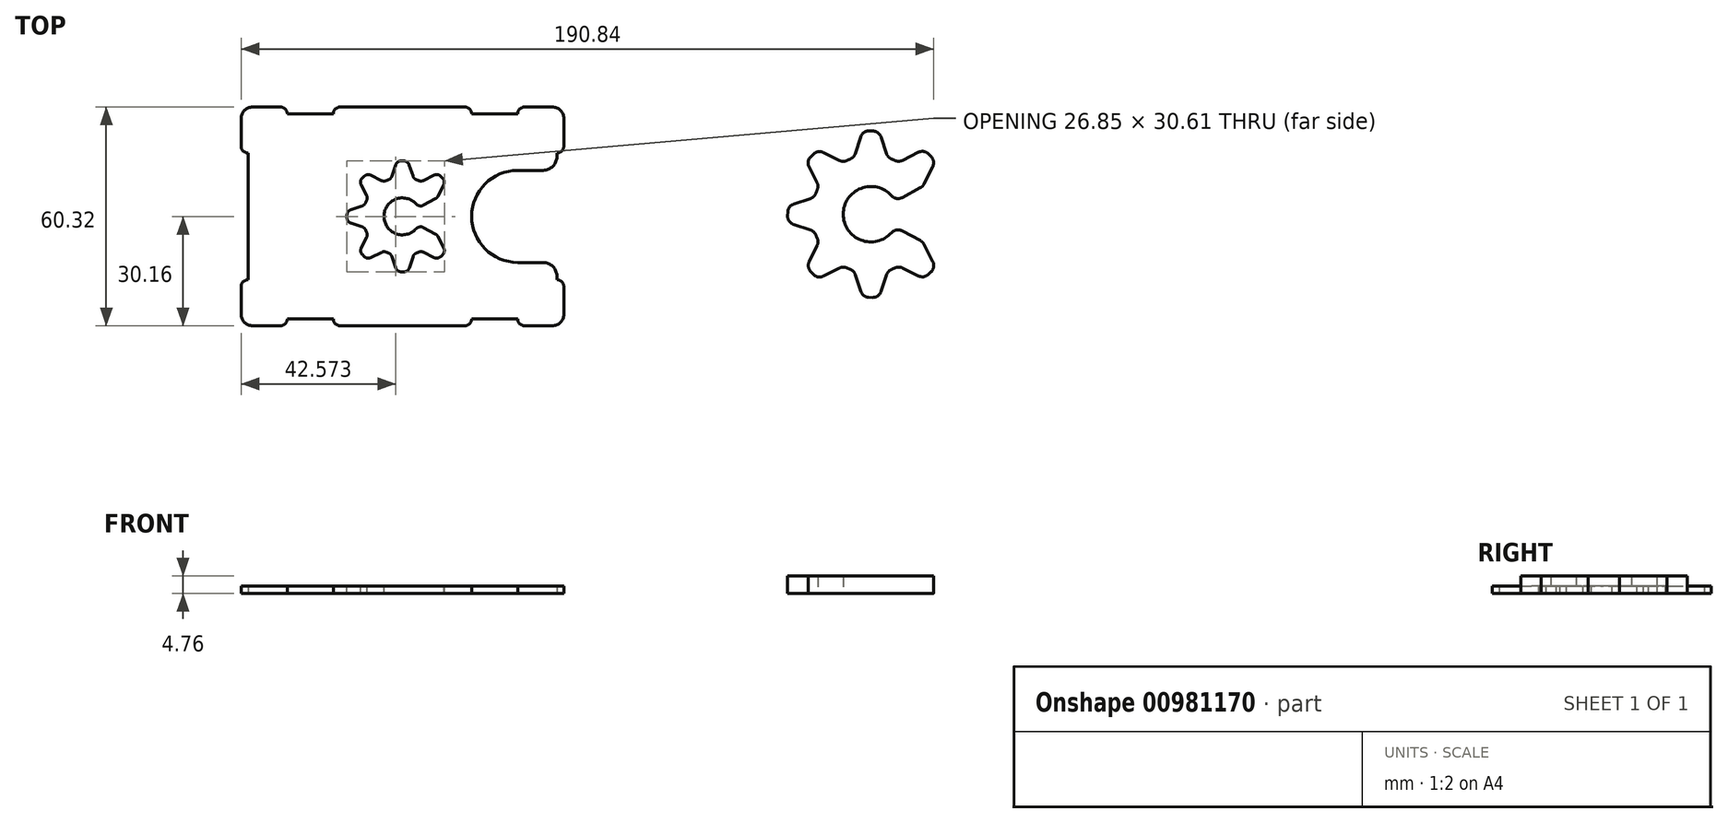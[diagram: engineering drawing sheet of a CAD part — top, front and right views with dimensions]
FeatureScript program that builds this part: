
annotation { "Feature Type Name" : "Feature", "Feature Type Description" : "" }
export const myFeature = defineFeature(function(context is Context, id is Id, definition is map)
    precondition{}
    {
        {
            var Q0;
            Q0=qCreatedBy(makeId("Top.planeOp"),FACE);
            var sketch = newSketch(context, id + "F0", { "sketchPlane" : qUnion([Q0])});
            skLineSegment(sketch, "E0.bottom", {"start": v(39.69, -26.99) * mm, "end": v(-39.69, -26.99) * mm, "construction": true});
            skLineSegment(sketch, "E0.top", {"start": v(39.69, 26.99) * mm, "end": v(-39.69, 26.99) * mm, "construction": true});
            skLineSegment(sketch, "E0.left", {"start": v(42.86, -23.81) * mm, "end": v(42.86, 23.81) * mm, "construction": true});
            skLineSegment(sketch, "E0.right", {"start": v(-42.86, -23.81) * mm, "end": v(-42.86, 23.81) * mm, "construction": true});
            skPoint(sketch, "E0.middle", {"position": v(0, 0) * mm});
            skPoint(sketch, "E1.visualSharp", {"position": v(-42.86, 26.99) * mm});
            skArc(sketch, "E1.filletArc", {"start": v(-39.69, 26.99) * mm, "mid": v(-41.93, 26.06) * mm, "end": v(-42.86, 23.81) * mm, "construction": true});
            skPoint(sketch, "E2.visualSharp", {"position": v(42.86, 26.99) * mm});
            skArc(sketch, "E2.filletArc", {"start": v(42.86, 23.81) * mm, "mid": v(41.93, 26.06) * mm, "end": v(39.69, 26.99) * mm, "construction": true});
            skPoint(sketch, "E3.visualSharp", {"position": v(42.86, -26.99) * mm});
            skArc(sketch, "E3.filletArc", {"start": v(39.69, -26.99) * mm, "mid": v(41.93, -26.06) * mm, "end": v(42.86, -23.81) * mm, "construction": true});
            skPoint(sketch, "E4.visualSharp", {"position": v(-42.86, -26.99) * mm});
            skArc(sketch, "E4.filletArc", {"start": v(-42.86, -23.81) * mm, "mid": v(-41.93, -26.06) * mm, "end": v(-39.69, -26.99) * mm, "construction": true});
            skLineSegment(sketch, "E5.bottom", {"start": v(41.28, -30.16) * mm, "end": v(31.75, -30.16) * mm});
            skLineSegment(sketch, "E5.top", {"start": v(41.28, 30.16) * mm, "end": v(31.75, 30.16) * mm});
            skLineSegment(sketch, "E5.left", {"start": v(44.45, -26.99) * mm, "end": v(44.45, -17.46) * mm});
            skLineSegment(sketch, "E5.right", {"start": v(-44.45, -26.99) * mm, "end": v(-44.45, -17.46) * mm});
            skPoint(sketch, "E6.visualSharp", {"position": v(44.45, 30.16) * mm});
            skArc(sketch, "E6.filletArc", {"start": v(44.45, 26.99) * mm, "mid": v(43.52, 29.23) * mm, "end": v(41.28, 30.16) * mm});
            skPoint(sketch, "E7.visualSharp", {"position": v(44.45, -30.16) * mm});
            skArc(sketch, "E7.filletArc", {"start": v(41.28, -30.16) * mm, "mid": v(43.52, -29.23) * mm, "end": v(44.45, -26.99) * mm});
            skPoint(sketch, "E8.visualSharp", {"position": v(-44.45, -30.16) * mm});
            skArc(sketch, "E8.filletArc", {"start": v(-44.45, -26.99) * mm, "mid": v(-43.52, -29.23) * mm, "end": v(-41.28, -30.16) * mm});
            skPoint(sketch, "E9.visualSharp", {"position": v(-44.45, 30.16) * mm});
            skArc(sketch, "E9.filletArc", {"start": v(-41.28, 30.16) * mm, "mid": v(-43.52, 29.23) * mm, "end": v(-44.45, 26.99) * mm});
            skLineSegment(sketch, "E10.top", {"start": v(-19.05, 28.26) * mm, "end": v(-31.75, 28.26) * mm});
            skLineSegment(sketch, "E10.left", {"start": v(-19.05, 30.16) * mm, "end": v(-19.05, 28.26) * mm});
            skLineSegment(sketch, "E10.right", {"start": v(-31.75, 30.16) * mm, "end": v(-31.75, 28.26) * mm});
            skPoint(sketch, "E10.middle", {"position": v(-25.4, 30.16) * mm});
            skLineSegment(sketch, "E11.top", {"start": v(31.75, 28.26) * mm, "end": v(19.05, 28.26) * mm});
            skLineSegment(sketch, "E11.left", {"start": v(31.75, 30.16) * mm, "end": v(31.75, 28.26) * mm});
            skLineSegment(sketch, "E11.right", {"start": v(19.05, 30.16) * mm, "end": v(19.05, 28.26) * mm});
            skPoint(sketch, "E11.middle", {"position": v(25.4, 30.16) * mm});
            skLineSegment(sketch, "E12.top", {"start": v(31.75, -28.26) * mm, "end": v(19.05, -28.26) * mm});
            skLineSegment(sketch, "E12.left", {"start": v(31.75, -30.16) * mm, "end": v(31.75, -28.26) * mm});
            skLineSegment(sketch, "E12.right", {"start": v(19.05, -30.16) * mm, "end": v(19.05, -28.26) * mm});
            skPoint(sketch, "E12.middle", {"position": v(25.4, -30.16) * mm});
            skLineSegment(sketch, "E13.top", {"start": v(-19.05, -28.26) * mm, "end": v(-31.75, -28.26) * mm});
            skLineSegment(sketch, "E13.left", {"start": v(-19.05, -30.16) * mm, "end": v(-19.05, -28.26) * mm});
            skLineSegment(sketch, "E13.right", {"start": v(-31.75, -30.16) * mm, "end": v(-31.75, -28.26) * mm});
            skPoint(sketch, "E13.middle", {"position": v(-25.4, -30.16) * mm});
            skLineSegment(sketch, "E14.trimOffspring", {"start": v(-31.75, 30.16) * mm, "end": v(-41.28, 30.16) * mm});
            skLineSegment(sketch, "E15.trimOffspring", {"start": v(19.05, 30.16) * mm, "end": v(-19.05, 30.16) * mm});
            skPoint(sketch, "E16.orphan", {"position": v(31.75, 32.07) * mm});
            skPoint(sketch, "E17.orphan", {"position": v(19.05, 32.07) * mm});
            skPoint(sketch, "E18.orphan", {"position": v(-31.75, 32.07) * mm});
            skPoint(sketch, "E19.orphan", {"position": v(-19.05, 32.07) * mm});
            skPoint(sketch, "E13.bottom.end.orphan", {"position": v(-31.75, -32.07) * mm});
            skPoint(sketch, "E13.bottom.start.orphan", {"position": v(-19.05, -32.07) * mm});
            skLineSegment(sketch, "E20.trimOffspring", {"start": v(-31.75, -30.16) * mm, "end": v(-41.28, -30.16) * mm});
            skLineSegment(sketch, "E21.trimOffspring", {"start": v(19.05, -30.16) * mm, "end": v(-19.05, -30.16) * mm});
            skPoint(sketch, "E12.bottom.end.orphan", {"position": v(19.05, -32.07) * mm});
            skPoint(sketch, "E12.bottom.start.orphan", {"position": v(31.75, -32.07) * mm});
            skLineSegment(sketch, "E22.bottom", {"start": v(44.45, -17.46) * mm, "end": v(42.55, -17.46) * mm});
            skLineSegment(sketch, "E22.top", {"start": v(44.45, 17.46) * mm, "end": v(42.55, 17.46) * mm});
            skLineSegment(sketch, "E22.right", {"start": v(42.55, -17.46) * mm, "end": v(42.55, -12.7) * mm});
            skPoint(sketch, "E22.middle", {"position": v(44.45, 0) * mm});
            skLineSegment(sketch, "E23.trimOffspring", {"start": v(44.45, 17.46) * mm, "end": v(44.45, 26.99) * mm});
            skLineSegment(sketch, "E24.bottom", {"start": v(-44.45, 17.46) * mm, "end": v(-42.55, 17.46) * mm});
            skLineSegment(sketch, "E24.top", {"start": v(-44.45, -17.46) * mm, "end": v(-42.55, -17.46) * mm});
            skLineSegment(sketch, "E24.right", {"start": v(-42.55, 17.46) * mm, "end": v(-42.55, -17.46) * mm});
            skPoint(sketch, "E24.middle", {"position": v(-44.45, 0) * mm});
            skLineSegment(sketch, "E25.trimOffspring", {"start": v(-44.45, 17.46) * mm, "end": v(-44.45, 26.99) * mm});
            skPoint(sketch, "E24.left.start.orphan", {"position": v(-46.36, 17.46) * mm});
            skPoint(sketch, "E26.orphan", {"position": v(-46.36, -17.46) * mm});
            skPoint(sketch, "E22.left.start.orphan", {"position": v(46.36, -17.46) * mm});
            skPoint(sketch, "E27.orphan", {"position": v(46.36, 17.46) * mm});
            skLineSegment(sketch, "E28", {"start": v(44.45, 0) * mm, "end": v(31.75, 0) * mm});
            skArc(sketch, "E29.0.endCap", {"start": v(31.75, -12.7) * mm, "mid": v(19.05, 0) * mm, "end": v(31.75, 12.7) * mm});
            skLineSegment(sketch, "E29.0.right", {"start": v(42.55, 12.7) * mm, "end": v(31.75, 12.7) * mm});
            skLineSegment(sketch, "E30.trimOffspring", {"start": v(42.55, 12.7) * mm, "end": v(42.55, 17.46) * mm});
            skLineSegment(sketch, "E31.trimOffspring", {"start": v(42.55, -12.7) * mm, "end": v(31.75, -12.7) * mm});
            skSolve(sketch);
        }
        {
            var Q0;
            Q0=makeQuery(id+"F0.imprint","IMPRINT",FACE,{"disambiguationData":[TD([[makeQuery(id+"F0.imprint","IMPRINT",EDGE,{"derivedFrom":sQuery(id+"F0.wireOp",EDGE,"E5.bottom")}),-1.0]])]});
            extrude(context, id + "F1", {"entities" : qUnion([Q0]), "depth" : 2.03 * mm, "offsetDistance" : 25.4 * mm});
        }
        {
            var Q0;
            Q0=makeQuery(id+"F1.opExtrude","CAP_FACE",FACE,{"disambiguationData":[OSD([sQuery(id+"F0.wireOp",EDGE,"E5.bottom"),sQuery(id+"F0.wireOp",EDGE,"E5.top"),sQuery(id+"F0.wireOp",EDGE,"E5.left"),sQuery(id+"F0.wireOp",EDGE,"E5.right"),sQuery(id+"F0.wireOp",EDGE,"E6.filletArc"),sQuery(id+"F0.wireOp",EDGE,"E7.filletArc"),sQuery(id+"F0.wireOp",EDGE,"E8.filletArc"),sQuery(id+"F0.wireOp",EDGE,"E9.filletArc"),sQuery(id+"F0.wireOp",EDGE,"E10.top"),sQuery(id+"F0.wireOp",EDGE,"E10.left"),sQuery(id+"F0.wireOp",EDGE,"E10.right"),sQuery(id+"F0.wireOp",EDGE,"E11.top"),sQuery(id+"F0.wireOp",EDGE,"E11.left"),sQuery(id+"F0.wireOp",EDGE,"E11.right"),sQuery(id+"F0.wireOp",EDGE,"E12.top"),sQuery(id+"F0.wireOp",EDGE,"E12.left"),sQuery(id+"F0.wireOp",EDGE,"E12.right"),sQuery(id+"F0.wireOp",EDGE,"E13.top"),sQuery(id+"F0.wireOp",EDGE,"E13.left"),sQuery(id+"F0.wireOp",EDGE,"E13.right"),sQuery(id+"F0.wireOp",EDGE,"E14.trimOffspring"),sQuery(id+"F0.wireOp",EDGE,"E15.trimOffspring"),sQuery(id+"F0.wireOp",EDGE,"E20.trimOffspring"),sQuery(id+"F0.wireOp",EDGE,"E21.trimOffspring"),sQuery(id+"F0.wireOp",EDGE,"E22.bottom"),sQuery(id+"F0.wireOp",EDGE,"E22.top"),sQuery(id+"F0.wireOp",EDGE,"E22.right"),sQuery(id+"F0.wireOp",EDGE,"E23.trimOffspring"),sQuery(id+"F0.wireOp",EDGE,"E24.bottom"),sQuery(id+"F0.wireOp",EDGE,"E24.top"),sQuery(id+"F0.wireOp",EDGE,"E24.right"),sQuery(id+"F0.wireOp",EDGE,"E25.trimOffspring"),sQuery(id+"F0.wireOp",EDGE,"E29.0.endCap"),sQuery(id+"F0.wireOp",EDGE,"E29.0.right"),sQuery(id+"F0.wireOp",EDGE,"E30.trimOffspring"),sQuery(id+"F0.wireOp",EDGE,"E31.trimOffspring")])],"isStart":false});
            var sketch = newSketch(context, id + "F2", { "sketchPlane" : qUnion([Q0])});
            skLineSegment(sketch, "E32.0", {"start": v(11.34, 8.72) * mm, "end": v(9.77, 5.56) * mm});
            skLineSegment(sketch, "E33.0", {"start": v(10.6, 11.04) * mm, "end": v(11.08, 10.53) * mm});
            skLineSegment(sketch, "E34.0", {"start": v(5.8, 9.9) * mm, "end": v(8.7, 11.38) * mm});
            skArc(sketch, "E35", {"start": v(3.79, 3.4) * mm, "mid": v(-5.1, 0) * mm, "end": v(3.79, -3.4) * mm});
            skArc(sketch, "E36", {"start": v(4.43, 9.87) * mm, "mid": v(4.14, 10) * mm, "end": v(3.84, 10.12) * mm});
            skLineSegment(sketch, "E37", {"start": v(10.8, 10.82) * mm, "end": v(0, 0) * mm, "construction": true});
            skLineSegment(sketch, "E38.1.0", {"start": v(1.85, 14.19) * mm, "end": v(2.89, 11.1) * mm});
            skLineSegment(sketch, "E38.1.1", {"start": v(-2.9, 11.11) * mm, "end": v(-1.89, 14.2) * mm});
            skLineSegment(sketch, "E38.1.2", {"start": v(-0.32, 15.3) * mm, "end": v(0.39, 15.28) * mm});
            skLineSegment(sketch, "E38.2.0", {"start": v(-8.72, 11.34) * mm, "end": v(-5.8, 9.9) * mm});
            skLineSegment(sketch, "E38.2.1", {"start": v(-9.9, 5.8) * mm, "end": v(-11.38, 8.7) * mm});
            skLineSegment(sketch, "E38.2.2", {"start": v(-11.04, 10.6) * mm, "end": v(-10.53, 11.08) * mm});
            skLineSegment(sketch, "E38.3.0", {"start": v(-14.19, 1.85) * mm, "end": v(-11.1, 2.89) * mm});
            skLineSegment(sketch, "E38.3.1", {"start": v(-11.11, -2.9) * mm, "end": v(-14.2, -1.89) * mm});
            skLineSegment(sketch, "E38.3.2", {"start": v(-15.3, -0.32) * mm, "end": v(-15.28, 0.39) * mm});
            skLineSegment(sketch, "E38.4.0", {"start": v(-11.34, -8.72) * mm, "end": v(-9.9, -5.8) * mm});
            skLineSegment(sketch, "E38.4.1", {"start": v(-5.8, -9.9) * mm, "end": v(-8.7, -11.38) * mm});
            skLineSegment(sketch, "E38.4.2", {"start": v(-10.6, -11.04) * mm, "end": v(-11.08, -10.53) * mm});
            skLineSegment(sketch, "E38.5.0", {"start": v(-1.85, -14.19) * mm, "end": v(-2.89, -11.1) * mm});
            skLineSegment(sketch, "E38.5.1", {"start": v(2.9, -11.11) * mm, "end": v(1.89, -14.2) * mm});
            skLineSegment(sketch, "E38.5.2", {"start": v(0.32, -15.3) * mm, "end": v(-0.39, -15.28) * mm});
            skLineSegment(sketch, "E38.6.0", {"start": v(8.72, -11.34) * mm, "end": v(5.8, -9.9) * mm});
            skLineSegment(sketch, "E38.6.1", {"start": v(9.77, -5.55) * mm, "end": v(11.38, -8.7) * mm});
            skLineSegment(sketch, "E38.6.2", {"start": v(11.04, -10.6) * mm, "end": v(10.53, -11.08) * mm});
            skLineSegment(sketch, "E39", {"start": v(5.73, -3.06) * mm, "end": v(9.1, -4.86) * mm});
            skLineSegment(sketch, "E40", {"start": v(5.73, 3.06) * mm, "end": v(9.1, 4.86) * mm});
            skArc(sketch, "E41.trimOffspring", {"start": v(3.85, -10.11) * mm, "mid": v(4.15, -10) * mm, "end": v(4.44, -9.87) * mm});
            skArc(sketch, "E42.trimOffspring", {"start": v(-4.43, -9.87) * mm, "mid": v(-4.14, -10) * mm, "end": v(-3.84, -10.12) * mm});
            skArc(sketch, "E43.trimOffspring", {"start": v(-10.11, -3.85) * mm, "mid": v(-10, -4.15) * mm, "end": v(-9.87, -4.44) * mm});
            skArc(sketch, "E44.trimOffspring", {"start": v(-9.87, 4.43) * mm, "mid": v(-10, 4.14) * mm, "end": v(-10.12, 3.84) * mm});
            skArc(sketch, "E45.trimOffspring", {"start": v(-3.85, 10.11) * mm, "mid": v(-4.15, 10) * mm, "end": v(-4.44, 9.87) * mm});
            skPoint(sketch, "E46.visualSharp", {"position": v(1.5, 15.25) * mm});
            skArc(sketch, "E46.filletArc", {"start": v(1.85, 14.19) * mm, "mid": v(1.3, 14.97) * mm, "end": v(0.39, 15.28) * mm});
            skPoint(sketch, "E47.visualSharp", {"position": v(-9.72, 11.84) * mm});
            skArc(sketch, "E47.filletArc", {"start": v(-8.72, 11.34) * mm, "mid": v(-9.67, 11.5) * mm, "end": v(-10.53, 11.08) * mm});
            skPoint(sketch, "E48.visualSharp", {"position": v(-15.25, 1.5) * mm});
            skArc(sketch, "E48.filletArc", {"start": v(-14.19, 1.85) * mm, "mid": v(-14.97, 1.3) * mm, "end": v(-15.28, 0.39) * mm});
            skPoint(sketch, "E49.visualSharp", {"position": v(-11.84, -9.72) * mm});
            skArc(sketch, "E49.filletArc", {"start": v(-11.34, -8.72) * mm, "mid": v(-11.5, -9.67) * mm, "end": v(-11.08, -10.53) * mm});
            skPoint(sketch, "E50.visualSharp", {"position": v(-1.5, -15.25) * mm});
            skArc(sketch, "E50.filletArc", {"start": v(-1.85, -14.19) * mm, "mid": v(-1.3, -14.97) * mm, "end": v(-0.39, -15.28) * mm});
            skPoint(sketch, "E51.visualSharp", {"position": v(9.72, -11.84) * mm});
            skArc(sketch, "E51.filletArc", {"start": v(8.72, -11.34) * mm, "mid": v(9.67, -11.5) * mm, "end": v(10.53, -11.08) * mm});
            skPoint(sketch, "E52.visualSharp", {"position": v(4.5, -2.4) * mm});
            skArc(sketch, "E52.filletArc", {"start": v(5.73, -3.06) * mm, "mid": v(4.7, -2.9) * mm, "end": v(3.79, -3.4) * mm});
            skPoint(sketch, "E53.visualSharp", {"position": v(4.49, 2.4) * mm});
            skArc(sketch, "E53.filletArc", {"start": v(3.79, 3.4) * mm, "mid": v(4.7, 2.9) * mm, "end": v(5.73, 3.06) * mm});
            skPoint(sketch, "E54.visualSharp", {"position": v(1.51, -15.34) * mm});
            skArc(sketch, "E54.filletArc", {"start": v(0.32, -15.3) * mm, "mid": v(1.28, -15.01) * mm, "end": v(1.89, -14.2) * mm});
            skPoint(sketch, "E55.visualSharp", {"position": v(-9.78, -11.92) * mm});
            skArc(sketch, "E55.filletArc", {"start": v(-10.6, -11.04) * mm, "mid": v(-9.7, -11.52) * mm, "end": v(-8.7, -11.38) * mm});
            skPoint(sketch, "E56.visualSharp", {"position": v(-5.1, -9.54) * mm});
            skArc(sketch, "E56.filletArc", {"start": v(-4.43, -9.87) * mm, "mid": v(-5.12, -9.73) * mm, "end": v(-5.8, -9.9) * mm});
            skPoint(sketch, "E57.newPointA", {"position": v(-3.14, -10.35) * mm});
            skArc(sketch, "E57.filletArc", {"start": v(-2.89, -11.1) * mm, "mid": v(-3.25, -10.5) * mm, "end": v(-3.84, -10.12) * mm});
            skPoint(sketch, "E58.visualSharp", {"position": v(3.14, -10.35) * mm});
            skArc(sketch, "E58.filletArc", {"start": v(3.85, -10.11) * mm, "mid": v(3.26, -10.5) * mm, "end": v(2.9, -11.11) * mm});
            skPoint(sketch, "E59.newPointB", {"position": v(5.1, -9.54) * mm});
            skArc(sketch, "E59.filletArc", {"start": v(5.8, -9.9) * mm, "mid": v(5.13, -9.73) * mm, "end": v(4.44, -9.87) * mm});
            skPoint(sketch, "E60.visualSharp", {"position": v(11.92, -9.78) * mm});
            skArc(sketch, "E60.filletArc", {"start": v(11.04, -10.6) * mm, "mid": v(11.52, -9.7) * mm, "end": v(11.38, -8.7) * mm});
            skPoint(sketch, "E61.visualSharp", {"position": v(9.54, -5.1) * mm});
            skArc(sketch, "E61.filletArc", {"start": v(9.77, -5.55) * mm, "mid": v(9.49, -5.15) * mm, "end": v(9.1, -4.86) * mm});
            skPoint(sketch, "E62.visualSharp", {"position": v(-15.34, -1.51) * mm});
            skArc(sketch, "E62.filletArc", {"start": v(-15.3, -0.32) * mm, "mid": v(-15.01, -1.28) * mm, "end": v(-14.2, -1.89) * mm});
            skPoint(sketch, "E63.visualSharp", {"position": v(-10.35, -3.14) * mm});
            skArc(sketch, "E63.filletArc", {"start": v(-10.11, -3.85) * mm, "mid": v(-10.5, -3.26) * mm, "end": v(-11.11, -2.9) * mm});
            skPoint(sketch, "E64.newPointB", {"position": v(-9.54, -5.1) * mm});
            skArc(sketch, "E64.filletArc", {"start": v(-9.9, -5.8) * mm, "mid": v(-9.73, -5.13) * mm, "end": v(-9.87, -4.44) * mm});
            skPoint(sketch, "E65.newPointA", {"position": v(-10.35, 3.14) * mm});
            skArc(sketch, "E65.filletArc", {"start": v(-11.1, 2.89) * mm, "mid": v(-10.5, 3.25) * mm, "end": v(-10.12, 3.84) * mm});
            skPoint(sketch, "E66.visualSharp", {"position": v(-9.54, 5.1) * mm});
            skArc(sketch, "E66.filletArc", {"start": v(-9.87, 4.43) * mm, "mid": v(-9.73, 5.12) * mm, "end": v(-9.9, 5.8) * mm});
            skPoint(sketch, "E67.visualSharp", {"position": v(-11.92, 9.78) * mm});
            skArc(sketch, "E67.filletArc", {"start": v(-11.04, 10.6) * mm, "mid": v(-11.52, 9.7) * mm, "end": v(-11.38, 8.7) * mm});
            skPoint(sketch, "E68.newPointA", {"position": v(-5.1, 9.54) * mm});
            skArc(sketch, "E68.filletArc", {"start": v(-5.8, 9.9) * mm, "mid": v(-5.13, 9.73) * mm, "end": v(-4.44, 9.87) * mm});
            skPoint(sketch, "E69.visualSharp", {"position": v(-3.14, 10.35) * mm});
            skArc(sketch, "E69.filletArc", {"start": v(-3.85, 10.11) * mm, "mid": v(-3.26, 10.5) * mm, "end": v(-2.9, 11.11) * mm});
            skPoint(sketch, "E70.newPointB", {"position": v(3.14, 10.35) * mm});
            skArc(sketch, "E70.filletArc", {"start": v(2.89, 11.1) * mm, "mid": v(3.25, 10.5) * mm, "end": v(3.84, 10.12) * mm});
            skPoint(sketch, "E71.visualSharp", {"position": v(5.1, 9.54) * mm});
            skArc(sketch, "E71.filletArc", {"start": v(4.43, 9.87) * mm, "mid": v(5.12, 9.73) * mm, "end": v(5.8, 9.9) * mm});
            skPoint(sketch, "E72.visualSharp", {"position": v(-1.51, 15.34) * mm});
            skArc(sketch, "E72.filletArc", {"start": v(-0.32, 15.3) * mm, "mid": v(-1.28, 15.01) * mm, "end": v(-1.89, 14.2) * mm});
            skPoint(sketch, "E73.visualSharp", {"position": v(9.78, 11.92) * mm});
            skArc(sketch, "E73.filletArc", {"start": v(10.6, 11.04) * mm, "mid": v(9.7, 11.52) * mm, "end": v(8.7, 11.38) * mm});
            skPoint(sketch, "E74.visualSharp", {"position": v(11.84, 9.72) * mm});
            skArc(sketch, "E74.filletArc", {"start": v(11.34, 8.72) * mm, "mid": v(11.5, 9.67) * mm, "end": v(11.08, 10.53) * mm});
            skPoint(sketch, "E75.newPointA", {"position": v(9.54, 5.1) * mm});
            skArc(sketch, "E75.filletArc", {"start": v(9.1, 4.86) * mm, "mid": v(9.48, 5.16) * mm, "end": v(9.77, 5.56) * mm});
            skSolve(sketch);
        }
        {
            var Q0;
            Q0=qCreatedBy(makeId("Top.planeOp"),FACE);
            var sketch = newSketch(context, id + "F3", { "sketchPlane" : qUnion([Q0])});
            skLineSegment(sketch, "E76.0", {"start": v(140.41, 9.33) * mm, "end": v(138.84, 6.16) * mm});
            skLineSegment(sketch, "E77.0", {"start": v(139.67, 11.65) * mm, "end": v(140.15, 11.13) * mm});
            skLineSegment(sketch, "E78.0", {"start": v(134.88, 10.5) * mm, "end": v(137.78, 11.98) * mm});
            skArc(sketch, "E79", {"start": v(132.85, 4) * mm, "mid": v(123.98, 0.6) * mm, "end": v(132.86, -2.8) * mm});
            skArc(sketch, "E80", {"start": v(133.5, 10.47) * mm, "mid": v(133.2, 10.6) * mm, "end": v(132.9, 10.72) * mm});
            skLineSegment(sketch, "E81", {"start": v(139.88, 11.42) * mm, "end": v(129.07, 0.6) * mm, "construction": true});
            skLineSegment(sketch, "E82.1.0", {"start": v(130.92, 14.8) * mm, "end": v(131.96, 11.7) * mm});
            skLineSegment(sketch, "E82.1.1", {"start": v(126.17, 11.71) * mm, "end": v(127.18, 14.8) * mm});
            skLineSegment(sketch, "E82.1.2", {"start": v(128.75, 15.9) * mm, "end": v(129.46, 15.88) * mm});
            skLineSegment(sketch, "E82.2.0", {"start": v(120.35, 11.95) * mm, "end": v(123.26, 10.5) * mm});
            skLineSegment(sketch, "E82.2.1", {"start": v(119.17, 6.41) * mm, "end": v(117.7, 9.3) * mm});
            skLineSegment(sketch, "E82.2.2", {"start": v(118.03, 11.2) * mm, "end": v(118.54, 11.68) * mm});
            skLineSegment(sketch, "E82.3.0", {"start": v(114.88, 2.46) * mm, "end": v(117.97, 3.5) * mm});
            skLineSegment(sketch, "E82.3.1", {"start": v(117.96, -2.3) * mm, "end": v(114.87, -1.28) * mm});
            skLineSegment(sketch, "E82.3.2", {"start": v(113.77, 0.29) * mm, "end": v(113.79, 0.99) * mm});
            skLineSegment(sketch, "E82.4.0", {"start": v(117.72, -8.12) * mm, "end": v(119.18, -5.2) * mm});
            skLineSegment(sketch, "E82.4.1", {"start": v(123.26, -9.3) * mm, "end": v(120.36, -10.77) * mm});
            skLineSegment(sketch, "E82.4.2", {"start": v(118.47, -10.44) * mm, "end": v(118, -9.93) * mm});
            skLineSegment(sketch, "E82.5.0", {"start": v(127.22, -13.59) * mm, "end": v(126.18, -10.5) * mm});
            skLineSegment(sketch, "E82.5.1", {"start": v(131.96, -10.5) * mm, "end": v(130.96, -13.6) * mm});
            skLineSegment(sketch, "E82.5.2", {"start": v(129.38, -14.7) * mm, "end": v(128.68, -14.68) * mm});
            skLineSegment(sketch, "E82.6.0", {"start": v(137.8, -10.74) * mm, "end": v(134.88, -9.3) * mm});
            skLineSegment(sketch, "E82.6.1", {"start": v(138.84, -4.94) * mm, "end": v(140.44, -8.1) * mm});
            skLineSegment(sketch, "E82.6.2", {"start": v(140.11, -10) * mm, "end": v(139.6, -10.48) * mm});
            skLineSegment(sketch, "E83", {"start": v(134.8, -2.46) * mm, "end": v(138.17, -4.26) * mm});
            skLineSegment(sketch, "E84", {"start": v(134.8, 3.67) * mm, "end": v(138.16, 5.46) * mm});
            skArc(sketch, "E85.trimOffspring", {"start": v(132.92, -9.5) * mm, "mid": v(133.21, -9.4) * mm, "end": v(133.5, -9.26) * mm});
            skArc(sketch, "E86.trimOffspring", {"start": v(124.64, -9.27) * mm, "mid": v(124.93, -9.4) * mm, "end": v(125.23, -9.51) * mm});
            skArc(sketch, "E87.trimOffspring", {"start": v(118.96, -3.24) * mm, "mid": v(119.08, -3.54) * mm, "end": v(119.2, -3.84) * mm});
            skArc(sketch, "E88.trimOffspring", {"start": v(119.2, 5.03) * mm, "mid": v(119.07, 4.74) * mm, "end": v(118.95, 4.44) * mm});
            skArc(sketch, "E89.trimOffspring", {"start": v(125.22, 10.71) * mm, "mid": v(124.92, 10.6) * mm, "end": v(124.63, 10.47) * mm});
            skPoint(sketch, "E90.visualSharp", {"position": v(130.57, 15.85) * mm});
            skArc(sketch, "E90.filletArc", {"start": v(130.92, 14.8) * mm, "mid": v(130.36, 15.57) * mm, "end": v(129.46, 15.88) * mm});
            skPoint(sketch, "E91.visualSharp", {"position": v(119.35, 12.44) * mm});
            skArc(sketch, "E91.filletArc", {"start": v(120.35, 11.95) * mm, "mid": v(119.4, 12.1) * mm, "end": v(118.54, 11.68) * mm});
            skPoint(sketch, "E92.visualSharp", {"position": v(113.82, 2.1) * mm});
            skArc(sketch, "E92.filletArc", {"start": v(114.88, 2.46) * mm, "mid": v(114.1, 1.9) * mm, "end": v(113.79, 0.99) * mm});
            skPoint(sketch, "E93.visualSharp", {"position": v(117.23, -9.12) * mm});
            skArc(sketch, "E93.filletArc", {"start": v(117.72, -8.12) * mm, "mid": v(117.57, -9.07) * mm, "end": v(118, -9.93) * mm});
            skPoint(sketch, "E94.visualSharp", {"position": v(127.57, -14.64) * mm});
            skArc(sketch, "E94.filletArc", {"start": v(127.22, -13.59) * mm, "mid": v(127.78, -14.36) * mm, "end": v(128.68, -14.68) * mm});
            skPoint(sketch, "E95.visualSharp", {"position": v(138.79, -11.24) * mm});
            skArc(sketch, "E95.filletArc", {"start": v(137.8, -10.74) * mm, "mid": v(138.74, -10.9) * mm, "end": v(139.6, -10.48) * mm});
            skPoint(sketch, "E96.visualSharp", {"position": v(133.56, -1.8) * mm});
            skArc(sketch, "E96.filletArc", {"start": v(134.8, -2.46) * mm, "mid": v(133.77, -2.3) * mm, "end": v(132.86, -2.8) * mm});
            skPoint(sketch, "E97.visualSharp", {"position": v(133.56, 3) * mm});
            skArc(sketch, "E97.filletArc", {"start": v(132.85, 4) * mm, "mid": v(133.77, 3.5) * mm, "end": v(134.8, 3.67) * mm});
            skPoint(sketch, "E98.visualSharp", {"position": v(130.58, -14.74) * mm});
            skArc(sketch, "E98.filletArc", {"start": v(129.38, -14.7) * mm, "mid": v(130.35, -14.41) * mm, "end": v(130.96, -13.6) * mm});
            skPoint(sketch, "E99.visualSharp", {"position": v(119.3, -11.32) * mm});
            skArc(sketch, "E99.filletArc", {"start": v(118.47, -10.44) * mm, "mid": v(119.36, -10.92) * mm, "end": v(120.36, -10.77) * mm});
            skPoint(sketch, "E100.visualSharp", {"position": v(123.97, -8.94) * mm});
            skArc(sketch, "E100.filletArc", {"start": v(124.64, -9.27) * mm, "mid": v(123.95, -9.13) * mm, "end": v(123.26, -9.3) * mm});
            skPoint(sketch, "E101.newPointA", {"position": v(125.93, -9.74) * mm});
            skArc(sketch, "E101.filletArc", {"start": v(126.18, -10.5) * mm, "mid": v(125.82, -9.9) * mm, "end": v(125.23, -9.51) * mm});
            skPoint(sketch, "E102.visualSharp", {"position": v(132.21, -9.75) * mm});
            skArc(sketch, "E102.filletArc", {"start": v(132.92, -9.5) * mm, "mid": v(132.33, -9.9) * mm, "end": v(131.96, -10.5) * mm});
            skPoint(sketch, "E103.newPointB", {"position": v(134.16, -8.93) * mm});
            skArc(sketch, "E103.filletArc", {"start": v(134.88, -9.3) * mm, "mid": v(134.2, -9.12) * mm, "end": v(133.5, -9.26) * mm});
            skPoint(sketch, "E104.visualSharp", {"position": v(140.99, -9.17) * mm});
            skArc(sketch, "E104.filletArc", {"start": v(140.11, -10) * mm, "mid": v(140.6, -9.1) * mm, "end": v(140.44, -8.1) * mm});
            skPoint(sketch, "E105.visualSharp", {"position": v(138.61, -4.5) * mm});
            skArc(sketch, "E105.filletArc", {"start": v(138.84, -4.94) * mm, "mid": v(138.56, -4.55) * mm, "end": v(138.17, -4.26) * mm});
            skPoint(sketch, "E106.visualSharp", {"position": v(113.73, -0.91) * mm});
            skArc(sketch, "E106.filletArc", {"start": v(113.77, 0.29) * mm, "mid": v(114.06, -0.68) * mm, "end": v(114.87, -1.28) * mm});
            skPoint(sketch, "E107.visualSharp", {"position": v(118.72, -2.54) * mm});
            skArc(sketch, "E107.filletArc", {"start": v(118.96, -3.24) * mm, "mid": v(118.57, -2.66) * mm, "end": v(117.96, -2.3) * mm});
            skPoint(sketch, "E108.newPointB", {"position": v(119.53, -4.5) * mm});
            skArc(sketch, "E108.filletArc", {"start": v(119.18, -5.2) * mm, "mid": v(119.34, -4.52) * mm, "end": v(119.2, -3.84) * mm});
            skPoint(sketch, "E109.newPointA", {"position": v(118.72, 3.75) * mm});
            skArc(sketch, "E109.filletArc", {"start": v(117.97, 3.5) * mm, "mid": v(118.57, 3.86) * mm, "end": v(118.95, 4.44) * mm});
            skPoint(sketch, "E110.visualSharp", {"position": v(119.53, 5.7) * mm});
            skArc(sketch, "E110.filletArc", {"start": v(119.2, 5.03) * mm, "mid": v(119.34, 5.73) * mm, "end": v(119.17, 6.41) * mm});
            skPoint(sketch, "E111.visualSharp", {"position": v(117.15, 10.38) * mm});
            skArc(sketch, "E111.filletArc", {"start": v(118.03, 11.2) * mm, "mid": v(117.54, 10.31) * mm, "end": v(117.7, 9.3) * mm});
            skPoint(sketch, "E112.newPointA", {"position": v(123.98, 10.14) * mm});
            skArc(sketch, "E112.filletArc", {"start": v(123.26, 10.5) * mm, "mid": v(123.94, 10.33) * mm, "end": v(124.63, 10.47) * mm});
            skPoint(sketch, "E113.visualSharp", {"position": v(125.93, 10.96) * mm});
            skArc(sketch, "E113.filletArc", {"start": v(125.22, 10.71) * mm, "mid": v(125.81, 11.1) * mm, "end": v(126.17, 11.71) * mm});
            skPoint(sketch, "E114.newPointB", {"position": v(132.21, 10.95) * mm});
            skArc(sketch, "E114.filletArc", {"start": v(131.96, 11.7) * mm, "mid": v(132.32, 11.1) * mm, "end": v(132.9, 10.72) * mm});
            skPoint(sketch, "E115.visualSharp", {"position": v(134.17, 10.15) * mm});
            skArc(sketch, "E115.filletArc", {"start": v(133.5, 10.47) * mm, "mid": v(134.2, 10.33) * mm, "end": v(134.88, 10.5) * mm});
            skPoint(sketch, "E116.visualSharp", {"position": v(127.55, 15.94) * mm});
            skArc(sketch, "E116.filletArc", {"start": v(128.75, 15.9) * mm, "mid": v(127.78, 15.62) * mm, "end": v(127.18, 14.8) * mm});
            skPoint(sketch, "E117.visualSharp", {"position": v(138.85, 12.52) * mm});
            skArc(sketch, "E117.filletArc", {"start": v(139.67, 11.65) * mm, "mid": v(138.78, 12.13) * mm, "end": v(137.78, 11.98) * mm});
            skPoint(sketch, "E118.visualSharp", {"position": v(140.9, 10.32) * mm});
            skArc(sketch, "E118.filletArc", {"start": v(140.41, 9.33) * mm, "mid": v(140.56, 10.27) * mm, "end": v(140.15, 11.13) * mm});
            skPoint(sketch, "E119.newPointA", {"position": v(138.6, 5.7) * mm});
            skArc(sketch, "E119.filletArc", {"start": v(138.16, 5.46) * mm, "mid": v(138.55, 5.76) * mm, "end": v(138.84, 6.16) * mm});
            skSolve(sketch);
        }
        {
            var Q0;
            Q0 = qSketchRegion(id + "F2", true);
            extrude(context, id + "F4", {"entities" : qUnion([Q0]), "operationType" : NewBodyOperationType.REMOVE, "oppositeDirection" : true, "depth" : 25.4 * mm, "offsetDistance" : 25.4 * mm});
        }
        {
            var Q0;
            Q0 = qSketchRegion(id + "F3", true);
            extrude(context, id + "F5", {"entities" : qUnion([Q0]), "depth" : 3.17 * mm, "offsetDistance" : 25.4 * mm});
        }
        {
            var Q0;
            Q0=makeQuery(id+"F5.opExtrude","SWEPT_BODY",BODY,{"disambiguationData":[OSD([sQuery(id+"F3.wireOp",EDGE,"E76.0"),sQuery(id+"F3.wireOp",EDGE,"E77.0"),sQuery(id+"F3.wireOp",EDGE,"E78.0"),sQuery(id+"F3.wireOp",EDGE,"E79"),sQuery(id+"F3.wireOp",EDGE,"E80"),sQuery(id+"F3.wireOp",EDGE,"E82.1.0"),sQuery(id+"F3.wireOp",EDGE,"E82.1.1"),sQuery(id+"F3.wireOp",EDGE,"E82.1.2"),sQuery(id+"F3.wireOp",EDGE,"E82.2.0"),sQuery(id+"F3.wireOp",EDGE,"E82.2.1"),sQuery(id+"F3.wireOp",EDGE,"E82.2.2"),sQuery(id+"F3.wireOp",EDGE,"E82.3.0"),sQuery(id+"F3.wireOp",EDGE,"E82.3.1"),sQuery(id+"F3.wireOp",EDGE,"E82.3.2"),sQuery(id+"F3.wireOp",EDGE,"E82.4.0"),sQuery(id+"F3.wireOp",EDGE,"E82.4.1"),sQuery(id+"F3.wireOp",EDGE,"E82.4.2"),sQuery(id+"F3.wireOp",EDGE,"E82.5.0"),sQuery(id+"F3.wireOp",EDGE,"E82.5.1"),sQuery(id+"F3.wireOp",EDGE,"E82.5.2"),sQuery(id+"F3.wireOp",EDGE,"E82.6.0"),sQuery(id+"F3.wireOp",EDGE,"E82.6.1"),sQuery(id+"F3.wireOp",EDGE,"E82.6.2"),sQuery(id+"F3.wireOp",EDGE,"E83"),sQuery(id+"F3.wireOp",EDGE,"E84"),sQuery(id+"F3.wireOp",EDGE,"E85.trimOffspring"),sQuery(id+"F3.wireOp",EDGE,"E86.trimOffspring"),sQuery(id+"F3.wireOp",EDGE,"E87.trimOffspring"),sQuery(id+"F3.wireOp",EDGE,"E88.trimOffspring"),sQuery(id+"F3.wireOp",EDGE,"E89.trimOffspring"),sQuery(id+"F3.wireOp",EDGE,"E90.filletArc"),sQuery(id+"F3.wireOp",EDGE,"E91.filletArc"),sQuery(id+"F3.wireOp",EDGE,"E92.filletArc"),sQuery(id+"F3.wireOp",EDGE,"E93.filletArc"),sQuery(id+"F3.wireOp",EDGE,"E94.filletArc"),sQuery(id+"F3.wireOp",EDGE,"E95.filletArc"),sQuery(id+"F3.wireOp",EDGE,"E96.filletArc"),sQuery(id+"F3.wireOp",EDGE,"E97.filletArc"),sQuery(id+"F3.wireOp",EDGE,"E98.filletArc"),sQuery(id+"F3.wireOp",EDGE,"E99.filletArc"),sQuery(id+"F3.wireOp",EDGE,"E100.filletArc"),sQuery(id+"F3.wireOp",EDGE,"E101.filletArc"),sQuery(id+"F3.wireOp",EDGE,"E102.filletArc"),sQuery(id+"F3.wireOp",EDGE,"E103.filletArc"),sQuery(id+"F3.wireOp",EDGE,"E104.filletArc"),sQuery(id+"F3.wireOp",EDGE,"E105.filletArc"),sQuery(id+"F3.wireOp",EDGE,"E106.filletArc"),sQuery(id+"F3.wireOp",EDGE,"E107.filletArc"),sQuery(id+"F3.wireOp",EDGE,"E108.filletArc"),sQuery(id+"F3.wireOp",EDGE,"E109.filletArc"),sQuery(id+"F3.wireOp",EDGE,"E110.filletArc"),sQuery(id+"F3.wireOp",EDGE,"E111.filletArc"),sQuery(id+"F3.wireOp",EDGE,"E112.filletArc"),sQuery(id+"F3.wireOp",EDGE,"E113.filletArc"),sQuery(id+"F3.wireOp",EDGE,"E114.filletArc"),sQuery(id+"F3.wireOp",EDGE,"E115.filletArc"),sQuery(id+"F3.wireOp",EDGE,"E116.filletArc"),sQuery(id+"F3.wireOp",EDGE,"E117.filletArc"),sQuery(id+"F3.wireOp",EDGE,"E118.filletArc"),sQuery(id+"F3.wireOp",EDGE,"E119.filletArc")])]});
            var Q1;
            Q1=sQuery(id+"F3.wireOp",VERTEX,"E79.center");
            transform(context, id + "F6", {"entities" : qUnion([Q0]), "transformType" : TransformType.SCALE_UNIFORMLY, "scale" : 1.5, "scalePoint" : qUnion([Q1]), "makeCopy" : false});
        }
        {
            var Q0;
            Q0=makeQuery(id+"F1.opExtrude","SWEPT_EDGE",EDGE,{"disambiguationData":[OSD([sQuery(id+"F0.wireOp",EDGE,"E5.left"),sQuery(id+"F0.wireOp",EDGE,"E22.bottom")])]});
            var Q1;
            Q1=makeQuery(id+"F1.opExtrude","SWEPT_EDGE",EDGE,{"disambiguationData":[OSD([sQuery(id+"F0.wireOp",EDGE,"E22.top"),sQuery(id+"F0.wireOp",EDGE,"E23.trimOffspring")])]});
            var Q2;
            Q2=makeQuery(id+"F1.opExtrude","SWEPT_EDGE",EDGE,{"disambiguationData":[OSD([sQuery(id+"F0.wireOp",EDGE,"E12.right"),sQuery(id+"F0.wireOp",EDGE,"E21.trimOffspring")])]});
            var Q3;
            Q3=makeQuery(id+"F1.opExtrude","SWEPT_EDGE",EDGE,{"disambiguationData":[OSD([sQuery(id+"F0.wireOp",EDGE,"E5.bottom"),sQuery(id+"F0.wireOp",EDGE,"E12.left")])]});
            var Q4;
            Q4=makeQuery(id+"F1.opExtrude","SWEPT_EDGE",EDGE,{"disambiguationData":[OSD([sQuery(id+"F0.wireOp",EDGE,"E13.right"),sQuery(id+"F0.wireOp",EDGE,"E20.trimOffspring")])]});
            var Q5;
            Q5=makeQuery(id+"F1.opExtrude","SWEPT_EDGE",EDGE,{"disambiguationData":[OSD([sQuery(id+"F0.wireOp",EDGE,"E13.left"),sQuery(id+"F0.wireOp",EDGE,"E21.trimOffspring")])]});
            var Q6;
            Q6=makeQuery(id+"F1.opExtrude","SWEPT_EDGE",EDGE,{"disambiguationData":[OSD([sQuery(id+"F0.wireOp",EDGE,"E5.right"),sQuery(id+"F0.wireOp",EDGE,"E24.top")])]});
            var Q7;
            Q7=makeQuery(id+"F1.opExtrude","SWEPT_EDGE",EDGE,{"disambiguationData":[OSD([sQuery(id+"F0.wireOp",EDGE,"E24.bottom"),sQuery(id+"F0.wireOp",EDGE,"E25.trimOffspring")])]});
            var Q8;
            Q8=makeQuery(id+"F1.opExtrude","SWEPT_EDGE",EDGE,{"disambiguationData":[OSD([sQuery(id+"F0.wireOp",EDGE,"E10.left"),sQuery(id+"F0.wireOp",EDGE,"E15.trimOffspring")])]});
            var Q9;
            Q9=makeQuery(id+"F1.opExtrude","SWEPT_EDGE",EDGE,{"disambiguationData":[OSD([sQuery(id+"F0.wireOp",EDGE,"E10.right"),sQuery(id+"F0.wireOp",EDGE,"E14.trimOffspring")])]});
            var Q10;
            Q10=makeQuery(id+"F1.opExtrude","SWEPT_EDGE",EDGE,{"disambiguationData":[OSD([sQuery(id+"F0.wireOp",EDGE,"E5.top"),sQuery(id+"F0.wireOp",EDGE,"E11.left")])]});
            var Q11;
            Q11=makeQuery(id+"F1.opExtrude","SWEPT_EDGE",EDGE,{"disambiguationData":[OSD([sQuery(id+"F0.wireOp",EDGE,"E11.right"),sQuery(id+"F0.wireOp",EDGE,"E15.trimOffspring")])]});
            fillet(context, id + "F7", {"entities" : qUnion([Q0, Q1, Q2, Q3, Q4, Q5, Q6, Q7, Q8, Q9, Q10, Q11]), "radius" : 1.9 * mm, "tangentPropagation" : true, "allowEdgeOverflow" : false});
        }
        {
            var Q0;
            Q0=makeQuery(id+"F1.opExtrude","SWEPT_EDGE",EDGE,{"disambiguationData":[OSD([sQuery(id+"F0.wireOp",EDGE,"E29.0.right"),sQuery(id+"F0.wireOp",EDGE,"E30.trimOffspring")])]});
            var Q1;
            Q1=makeQuery(id+"F1.opExtrude","SWEPT_EDGE",EDGE,{"disambiguationData":[OSD([sQuery(id+"F0.wireOp",EDGE,"E22.right"),sQuery(id+"F0.wireOp",EDGE,"E31.trimOffspring")])]});
            fillet(context, id + "F8", {"entities" : qUnion([Q0, Q1]), "radius" : 3.8 * mm, "tangentPropagation" : true, "allowEdgeOverflow" : false});
        }
    });
